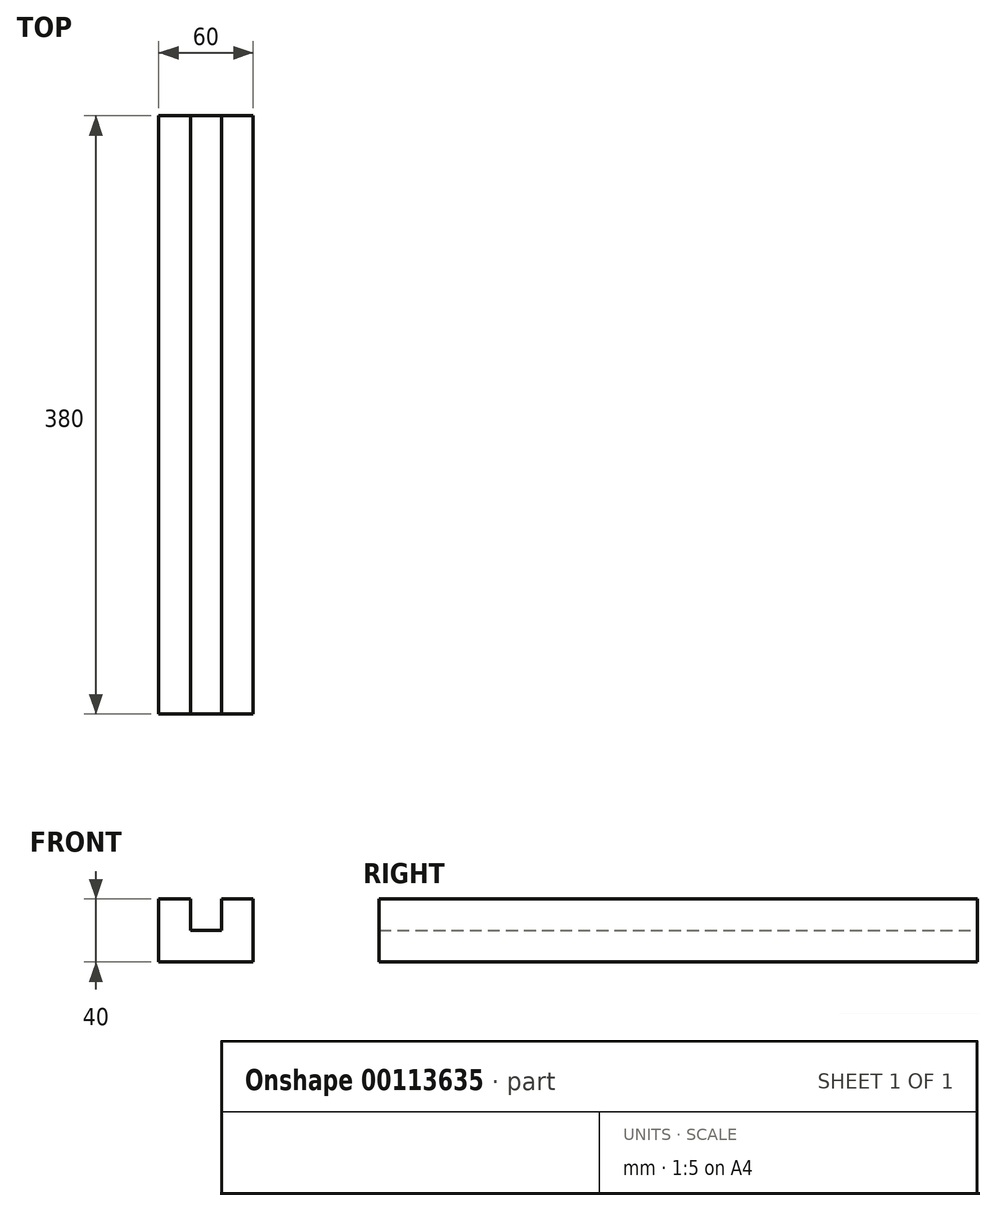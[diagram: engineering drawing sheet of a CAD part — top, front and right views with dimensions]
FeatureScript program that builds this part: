
annotation { "Feature Type Name" : "Feature", "Feature Type Description" : "" }
export const myFeature = defineFeature(function(context is Context, id is Id, definition is map)
    precondition{}
    {
        {
            var Q0;
            Q0=qCreatedBy(makeId("Front.planeOp"),FACE);
            var sketch = newSketch(context, id + "F0", { "sketchPlane" : qUnion([Q0])});
            skLineSegment(sketch, "E0.bottom", {"start": v(-27.5, 40) * mm, "end": v(-7.5, 40) * mm});
            skLineSegment(sketch, "E0.top", {"start": v(-27.5, 0) * mm, "end": v(32.5, 0) * mm});
            skLineSegment(sketch, "E0.left", {"start": v(-27.5, 40) * mm, "end": v(-27.5, 0) * mm});
            skLineSegment(sketch, "E0.right", {"start": v(32.5, 40) * mm, "end": v(32.5, 0) * mm});
            skLineSegment(sketch, "E1.top", {"start": v(-7.5, 20) * mm, "end": v(12.5, 20) * mm});
            skLineSegment(sketch, "E1.left", {"start": v(-7.5, 40) * mm, "end": v(-7.5, 20) * mm});
            skLineSegment(sketch, "E1.right", {"start": v(12.5, 40) * mm, "end": v(12.5, 20) * mm});
            skLineSegment(sketch, "E2.trimOffspring", {"start": v(12.5, 40) * mm, "end": v(32.5, 40) * mm});
            skSolve(sketch);
        }
        {
            var Q0;
            Q0 = qSketchRegion(id + "F0", true);
            extrude(context, id + "F1", {"entities" : qUnion([Q0]), "depth" : 380 * mm});
        }
    });
